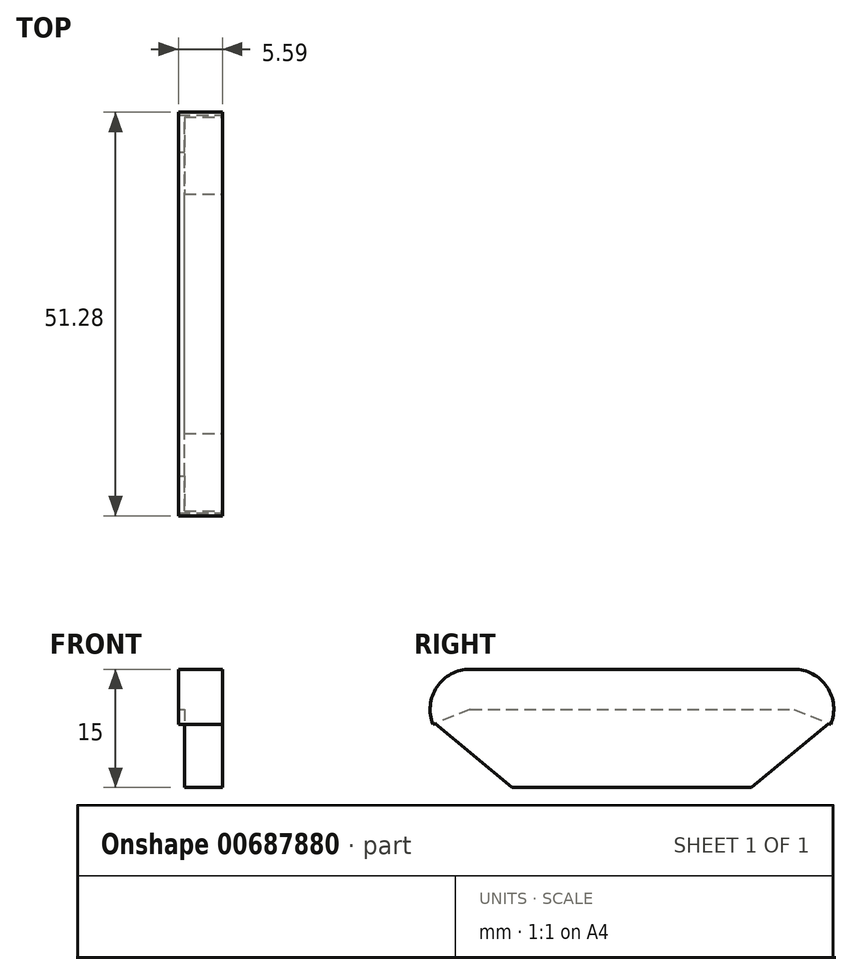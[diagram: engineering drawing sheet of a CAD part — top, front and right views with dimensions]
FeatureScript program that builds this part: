
annotation { "Feature Type Name" : "Feature", "Feature Type Description" : "" }
export const myFeature = defineFeature(function(context is Context, id is Id, definition is map)
    precondition{}
    {
        {
            var Q0;
            Q0=qCreatedBy(makeId("Right.planeOp"),FACE);
            var sketch = newSketch(context, id + "F0", { "sketchPlane" : qUnion([Q0])});
            skLineSegment(sketch, "E0", {"start": v(0, 5.37) * mm, "end": v(-20.57, 5.37) * mm});
            skLineSegment(sketch, "E1", {"start": v(0, 5.37) * mm, "end": v(20.57, 5.37) * mm});
            skLineSegment(sketch, "E2", {"start": v(-20.57, 5.37) * mm, "end": v(-20.57, 0.3) * mm});
            skLineSegment(sketch, "E3", {"start": v(-20.57, 0.3) * mm, "end": v(20.57, 0.3) * mm});
            skLineSegment(sketch, "E4", {"start": v(20.57, 0.3) * mm, "end": v(20.57, 5.37) * mm});
            skLineSegment(sketch, "E5", {"start": v(20.57, 0.3) * mm, "end": v(25.26, -1.63) * mm});
            skLineSegment(sketch, "E6", {"start": v(-20.57, 0.3) * mm, "end": v(-25.26, -1.63) * mm});
            skArc(sketch, "E7", {"start": v(-20.57, 5.37) * mm, "mid": v(-24.78, 3.12) * mm, "end": v(-25.25, -1.63) * mm});
            skArc(sketch, "E8", {"start": v(20.57, 5.37) * mm, "mid": v(24.78, 3.12) * mm, "end": v(25.26, -1.63) * mm});
            skLineSegment(sketch, "E9", {"start": v(25, -1.52) * mm, "end": v(15.21, -9.63) * mm});
            skLineSegment(sketch, "E10", {"start": v(-25, -1.52) * mm, "end": v(-15.2, -9.63) * mm});
            skLineSegment(sketch, "E11", {"start": v(-15.2, -9.63) * mm, "end": v(15.21, -9.63) * mm});
            skSolve(sketch);
        }
        {
            var Q0;
            {var subQ0=sQuery(id+"F0.wireOp",EDGE,"E2");Q0=makeQuery(id+"F0.imprint","IMPRINT",FACE,{"disambiguationData":[TD([[makeQuery(id+"F0.imprint","IMPRINT",EDGE,{"derivedFrom":subQ0}),-1.0]])]});}
            var Q1;
            Q1=makeQuery(id+"F0.imprint","IMPRINT",FACE,{"disambiguationData":[TD([[makeQuery(id+"F0.imprint","IMPRINT",EDGE,{"derivedFrom":sQuery(id+"F0.wireOp",EDGE,"E0")}),1.0]])]});
            var Q2;
            {var subQ0=sQuery(id+"F0.wireOp",EDGE,"E4");Q2=makeQuery(id+"F0.imprint","IMPRINT",FACE,{"disambiguationData":[TD([[makeQuery(id+"F0.imprint","IMPRINT",EDGE,{"derivedFrom":subQ0}),-1.0]])]});}
            extrude(context, id + "F1", {"entities" : qUnion([Q0, Q1, Q2]), "oppositeDirection" : true, "depth" : 5.6 * mm, "offsetDistance" : 25.4 * mm});
        }
        {
            var Q0;
            {var subQ2=sQuery(id+"F0.wireOp",EDGE,"E3");Q0=makeQuery(id+"F0.imprint","IMPRINT",FACE,{"disambiguationData":[TD([[makeQuery(id+"F0.imprint","IMPRINT",EDGE,{"derivedFrom":subQ2}),-1.0]])]});}
            extrude(context, id + "F2", {"entities" : qUnion([Q0]), "operationType" : NewBodyOperationType.ADD, "oppositeDirection" : true, "depth" : 4.83 * mm, "offsetDistance" : 25.4 * mm});
        }
    });
